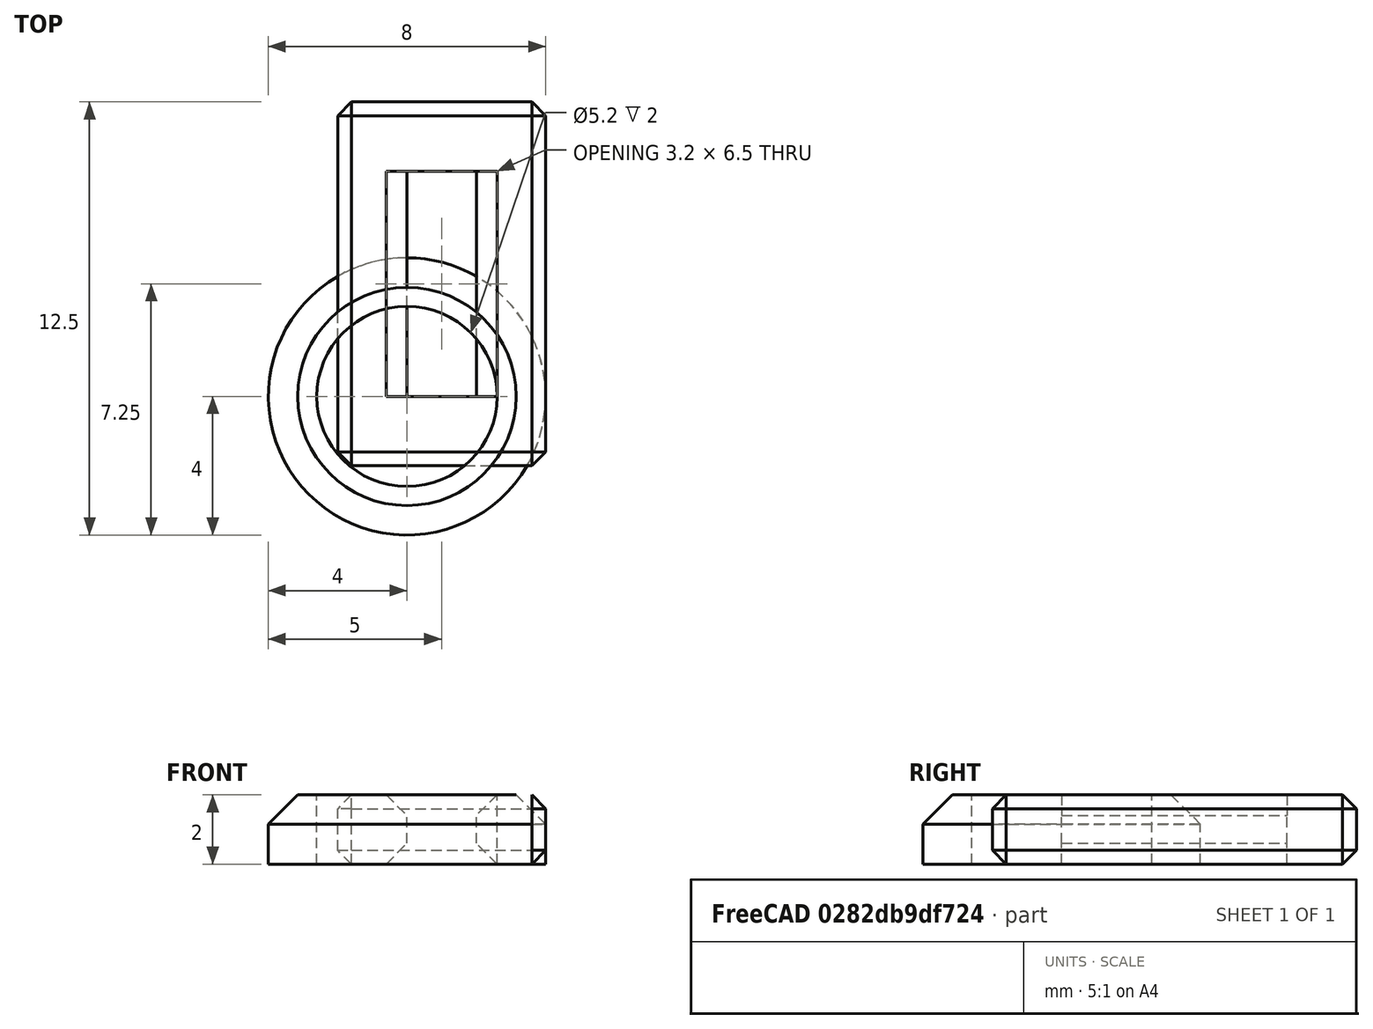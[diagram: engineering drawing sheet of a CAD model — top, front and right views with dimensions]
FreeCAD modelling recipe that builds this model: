
FCSTD DOCUMENT  (FreeCAD 0.19R24291 (Git))
Label: spacer-belt-mounter
License: All rights reserved
LicenseURL: http://en.wikipedia.org/wiki/All_rights_reserved
objects: Part::Chamfer×3, Part::Box×2, Part::FeaturePython×1, Part::Cut×1
note: 7 computed .brp shape members not serialized (recipe doc carries the construction recipe); baked Part::Feature solids carry a one-line shape summary decoded from their .brp

FEATURE [Part::FeaturePython] Tube  # WARN: FeaturePython — macro-defined, semantics opaque (R4)
  AttacherType = Attacher::AttachEngine3D
  Height = 2
  InnerRadius = 2.6
  OuterRadius = 4
FEATURE [Part::Chamfer] Chamfer
  Base = -> Tube
  Edges = 1 edges r=0.85: [Edge1]
FEATURE [Part::Box] Box  label="Cube"
  AttacherType = Attacher::AttachEngine3D
  Height = 2
  Length = 2
  Width = 6.5
FEATURE [Part::Box] Box001  label="Cube001"
  AttacherType = Attacher::AttachEngine3D
  Height = 2
  Length = 6
  Placement = pos=(-2,-2,0) rot=(0,0,1;0rad)
  Width = 10.5
FEATURE [Part::Cut] Cut
  Base = -> Box001
  Tool = -> Box
FEATURE [Part::Chamfer] Chamfer001
  Base = -> Cut
  Edges = 4 edges r=0.6: [Edge10,Edge12,Edge17,Edge19]
FEATURE [Part::Chamfer] Chamfer002
  Base = -> Chamfer001
  Edges = 12 edges r=0.4: [Edge9,Edge10,Edge11,Edge12,Edge33,Edge34,Edge35,Edge36,Edge37,Edge38,Edge39,Edge40]
